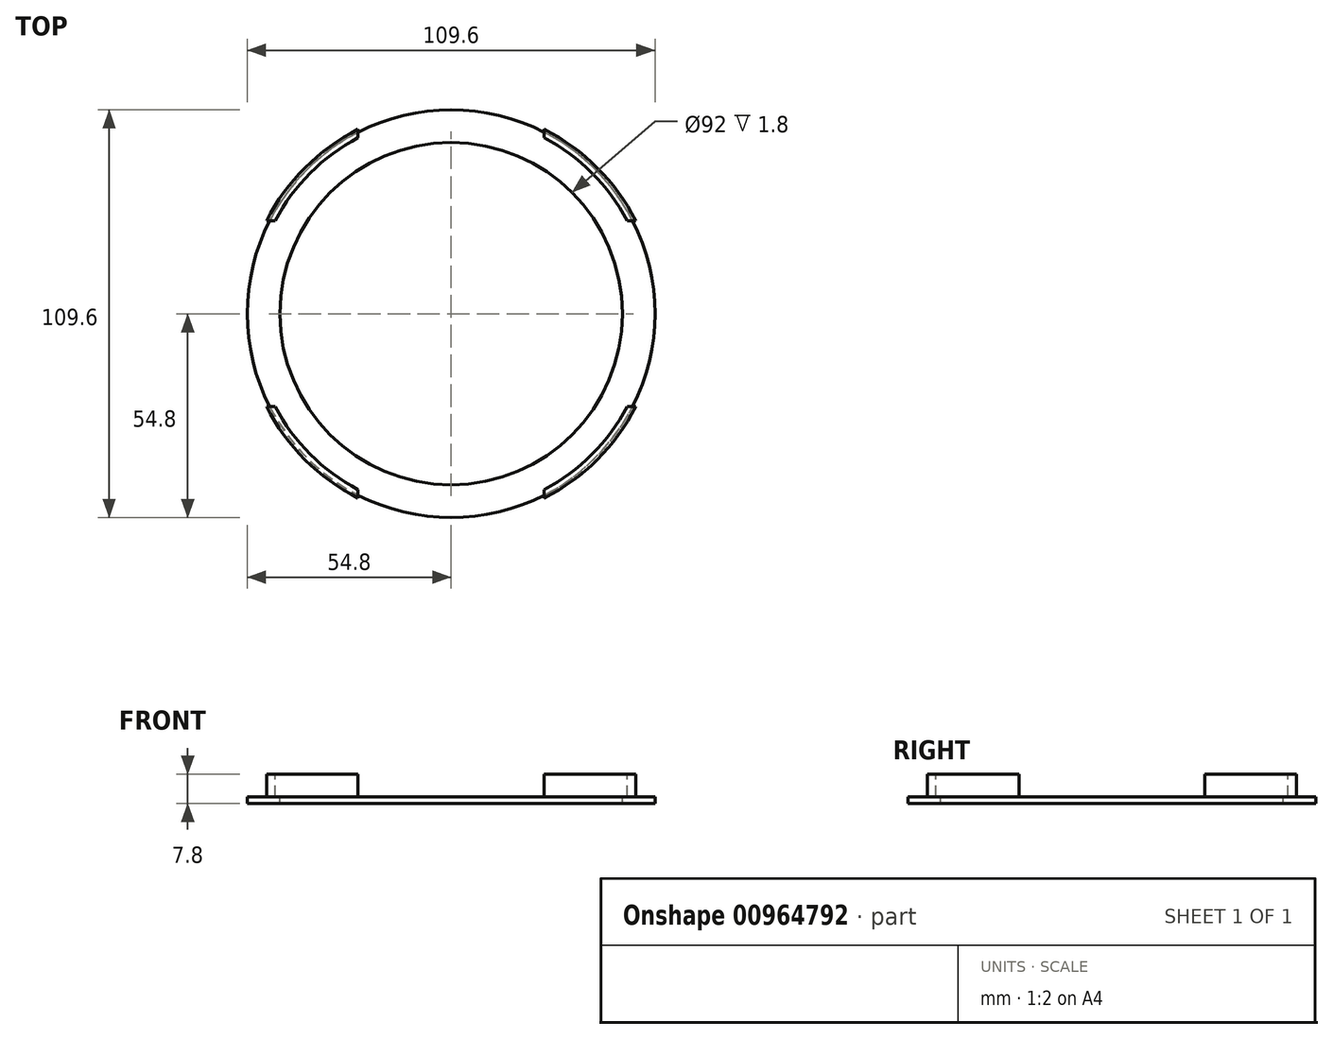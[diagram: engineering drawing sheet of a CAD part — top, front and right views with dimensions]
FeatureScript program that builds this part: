
annotation { "Feature Type Name" : "Feature", "Feature Type Description" : "" }
export const myFeature = defineFeature(function(context is Context, id is Id, definition is map)
    precondition{}
    {
        {
            var Q0;
            Q0=qCreatedBy(makeId("Top.planeOp"),FACE);
            var sketch = newSketch(context, id + "F0", { "sketchPlane" : qUnion([Q0])});
            skCircle(sketch, "E0", {"center": v(0, 0) * mm, "radius": 54.8 * mm});
            skSolve(sketch);
        }
        {
            var Q0;
            Q0=makeQuery(id+"F0.imprint","IMPRINT",FACE,{"disambiguationData":[TD([[makeQuery(id+"F0.imprint","IMPRINT",EDGE,{"derivedFrom":sQuery(id+"F0.wireOp",EDGE,"E0")}),1.0]])]});
            extrude(context, id + "F1", {"entities" : qUnion([Q0]), "depth" : 1.8 * mm, "offsetDistance" : 25 * mm});
        }
        {
            var Q0;
            Q0=makeQuery(id+"F1.opExtrude","CAP_FACE",FACE,{"disambiguationData":[OSD([sQuery(id+"F0.wireOp",EDGE,"E0")])],"isStart":false});
            var sketch = newSketch(context, id + "F2", { "sketchPlane" : qUnion([Q0])});
            skCircle(sketch, "E1", {"center": v(0, 0) * mm, "radius": 55.5 * mm});
            skSolve(sketch);
        }
        {
            var Q0;
            Q0 = qSketchRegion(id + "F2", true);
            extrude(context, id + "F3", {"entities" : qUnion([Q0]), "operationType" : NewBodyOperationType.ADD, "depth" : 6 * mm, "offsetDistance" : 25 * mm});
        }
        {
            var Q0;
            Q0=makeQuery(id+"F3.opExtrude","CAP_FACE",FACE,{"disambiguationData":[OSD([sQuery(id+"F2.wireOp",EDGE,"E1")])],"isStart":false});
            var sketch = newSketch(context, id + "F4", { "sketchPlane" : qUnion([Q0])});
            skLineSegment(sketch, "E2.bottom", {"start": v(-25, 62.5) * mm, "end": v(25, 62.5) * mm});
            skLineSegment(sketch, "E2.top", {"start": v(-25, -62.5) * mm, "end": v(25, -62.5) * mm});
            skLineSegment(sketch, "E2.left", {"start": v(-25, 62.5) * mm, "end": v(-25, -62.5) * mm});
            skLineSegment(sketch, "E2.right", {"start": v(25, 62.5) * mm, "end": v(25, -62.5) * mm});
            skPoint(sketch, "E2.middle", {"position": v(0, 0) * mm});
            skSolve(sketch);
        }
        {
            var Q0;
            Q0 = qSketchRegion(id + "F4", true);
            extrude(context, id + "F5", {"entities" : qUnion([Q0]), "operationType" : NewBodyOperationType.REMOVE, "oppositeDirection" : true, "depth" : 6 * mm, "offsetDistance" : 25 * mm});
        }
        {
            var Q0;
            {var subQ0=sQuery(id+"F2.wireOp",EDGE,"E1");Q0=makeQuery(id+"F5.boolean.opBoolean","SPLIT",FACE,{"disambiguationData":[TD([makeQuery(id+"F5.opExtrude","SWEPT_FACE",FACE,{"disambiguationData":[OSD([sQuery(id+"F4.wireOp",EDGE,"E2.left")])]})])],"derivedFrom":makeQuery(id+"F3.opExtrude","CAP_FACE",FACE,{"disambiguationData":[OSD([subQ0])],"isStart":false})});}
            var sketch = newSketch(context, id + "F6", { "sketchPlane" : qUnion([Q0])});
            skLineSegment(sketch, "E3.bottom", {"start": v(-60, 25) * mm, "end": v(60, 25) * mm});
            skLineSegment(sketch, "E3.top", {"start": v(-60, -25) * mm, "end": v(60, -25) * mm});
            skLineSegment(sketch, "E3.left", {"start": v(-60, 25) * mm, "end": v(-60, -25) * mm});
            skLineSegment(sketch, "E3.right", {"start": v(60, 25) * mm, "end": v(60, -25) * mm});
            skPoint(sketch, "E3.middle", {"position": v(0, 0) * mm});
            skSolve(sketch);
        }
        {
            var Q0;
            Q0 = qSketchRegion(id + "F6", true);
            extrude(context, id + "F7", {"entities" : qUnion([Q0]), "operationType" : NewBodyOperationType.REMOVE, "oppositeDirection" : true, "depth" : 6 * mm, "offsetDistance" : 25 * mm});
        }
        {
            var Q0;
            {var subQ0=sQuery(id+"F2.wireOp",EDGE,"E1");var subQ2=makeQuery(id+"F5.opExtrude","SWEPT_FACE",FACE,{"disambiguationData":[OSD([sQuery(id+"F4.wireOp",EDGE,"E2.left")])]});Q0=makeQuery(id+"F7.boolean.opBoolean","SPLIT",FACE,{"disambiguationData":[TD([makeQuery(id+"F7.opExtrude","SWEPT_FACE",FACE,{"disambiguationData":[OSD([sQuery(id+"F6.wireOp",EDGE,"E3.bottom")])]})])],"derivedFrom":makeQuery(id+"F5.boolean.opBoolean","SPLIT",FACE,{"disambiguationData":[TD([subQ2])],"derivedFrom":makeQuery(id+"F3.opExtrude","CAP_FACE",FACE,{"disambiguationData":[OSD([subQ0])],"isStart":false})})});}
            var sketch = newSketch(context, id + "F8", { "sketchPlane" : qUnion([Q0])});
            skCircle(sketch, "E4", {"center": v(0, 0) * mm, "radius": 53.5 * mm});
            skSolve(sketch);
        }
        {
            var Q0;
            Q0 = qSketchRegion(id + "F8", true);
            extrude(context, id + "F9", {"entities" : qUnion([Q0]), "operationType" : NewBodyOperationType.REMOVE, "oppositeDirection" : true, "depth" : 6 * mm, "offsetDistance" : 25 * mm});
        }
        {
            var Q0;
            Q0=makeQuery(id+"F9.boolean.opBoolean","MERGE",FACE,{"derivedFrom":[makeQuery(id+"F7.boolean.opBoolean","MERGE",FACE,{"derivedFrom":[makeQuery(id+"F5.boolean.opBoolean","COPY",FACE,{"derivedFrom":makeQuery(id+"F5.opExtrude","CAP_FACE",FACE,{"disambiguationData":[OSD([sQuery(id+"F4.wireOp",EDGE,"E2.bottom"),sQuery(id+"F4.wireOp",EDGE,"E2.top"),sQuery(id+"F4.wireOp",EDGE,"E2.left"),sQuery(id+"F4.wireOp",EDGE,"E2.right")])],"isStart":false})})],"fromTools":[makeQuery(id+"F7.opExtrude","CAP_FACE",FACE,{"disambiguationData":[OSD([sQuery(id+"F6.wireOp",EDGE,"E3.bottom"),sQuery(id+"F6.wireOp",EDGE,"E3.top"),sQuery(id+"F6.wireOp",EDGE,"E3.left"),sQuery(id+"F6.wireOp",EDGE,"E3.right")])],"isStart":false})]})],"fromTools":[makeQuery(id+"F9.opExtrude","CAP_FACE",FACE,{"disambiguationData":[OSD([sQuery(id+"F8.wireOp",EDGE,"E4")])],"isStart":false})]});
            var sketch = newSketch(context, id + "F10", { "sketchPlane" : qUnion([Q0])});
            skCircle(sketch, "E5", {"center": v(0, 0) * mm, "radius": 46 * mm});
            skSolve(sketch);
        }
        {
            var Q0;
            Q0 = qSketchRegion(id + "F10", true);
            extrude(context, id + "F11", {"entities" : qUnion([Q0]), "operationType" : NewBodyOperationType.REMOVE, "oppositeDirection" : true, "depth" : 25 * mm, "offsetDistance" : 25 * mm});
        }
    });
